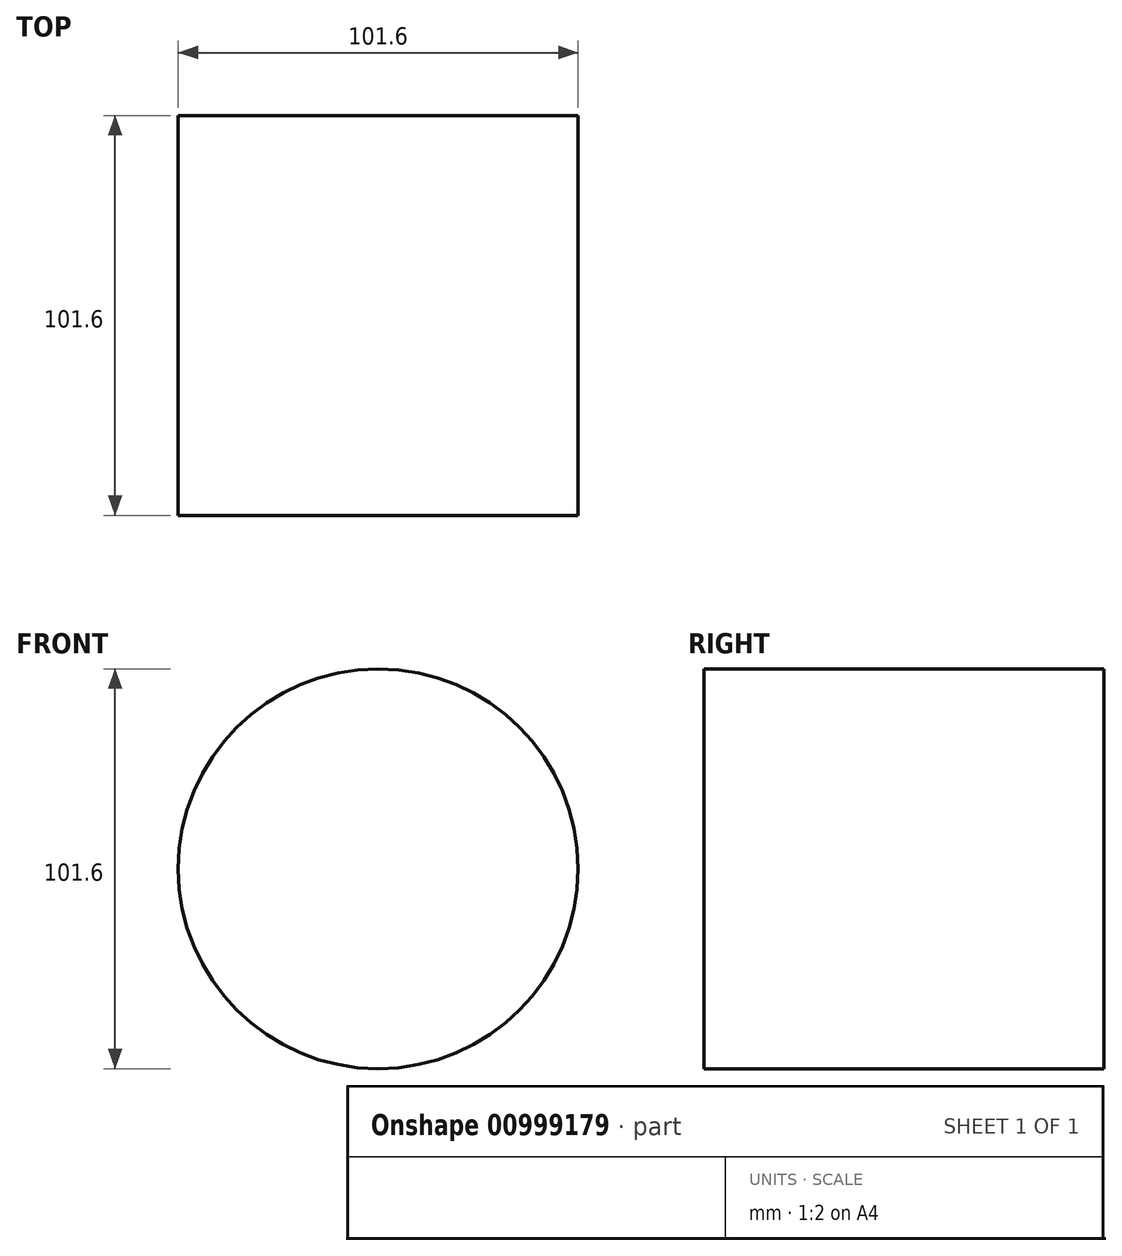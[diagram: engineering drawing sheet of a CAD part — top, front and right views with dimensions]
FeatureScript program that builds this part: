
annotation { "Feature Type Name" : "Feature", "Feature Type Description" : "" }
export const myFeature = defineFeature(function(context is Context, id is Id, definition is map)
    precondition{}
    {
        {
            var Q0;
            Q0=qCreatedBy(makeId("Front.planeOp"),FACE);
            var sketch = newSketch(context, id + "F0", { "sketchPlane" : qUnion([Q0])});
            skCircle(sketch, "E0", {"center": v(0, 0) * mm, "radius": 50.8 * mm});
            skSolve(sketch);
        }
        {
            var Q0;
            Q0=qSketchRegion(id+"F0",true);
            extrude(context, id + "F1", {"entities" : qUnion([Q0]), "depth" : 101.6 * mm, "offsetDistance" : 25.4 * mm});
        }
    });
